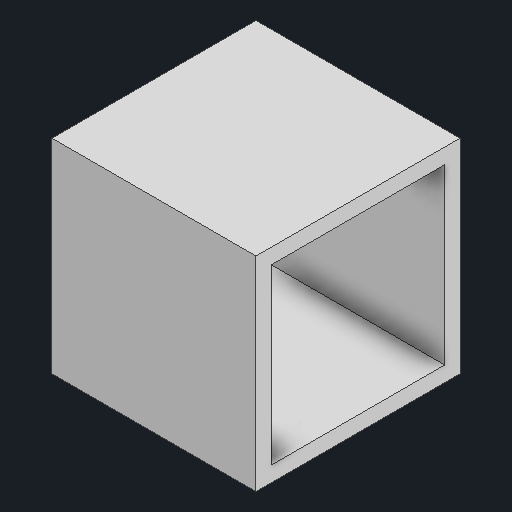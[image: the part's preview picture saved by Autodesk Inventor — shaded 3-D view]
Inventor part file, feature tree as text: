
AUTODESK INVENTOR PART (.ipt)
format: ipt  version: 2024 (Build 280153000, 153)  size: 124,416 bytes
history: native  units: mm
features: other x4, extrude x1, sketch x1, reference x1
ambient origin geometry x8: Origin, YZ Plane, XZ Plane, XY Plane, X Axis, Y Axis, Z Axis, Center Point
bodies: Body1 (feature_tree)
feature tree (7):
  other  "Твердое тело1"
  extrude  "Выдавливание1"  Depth=20.0mm
  sketch  "Эскиз1"
  reference  "Ссылка1"
  parser-record x1  (decoder bookkeeping rows leaked as tree rows — omitted from the tree; the rows remain in map.json)
  other  "base_assembly.iam"
  other  "main axis:1"
note: 1 file-system path scrubbed to <path> (originals preserved in map.json)
